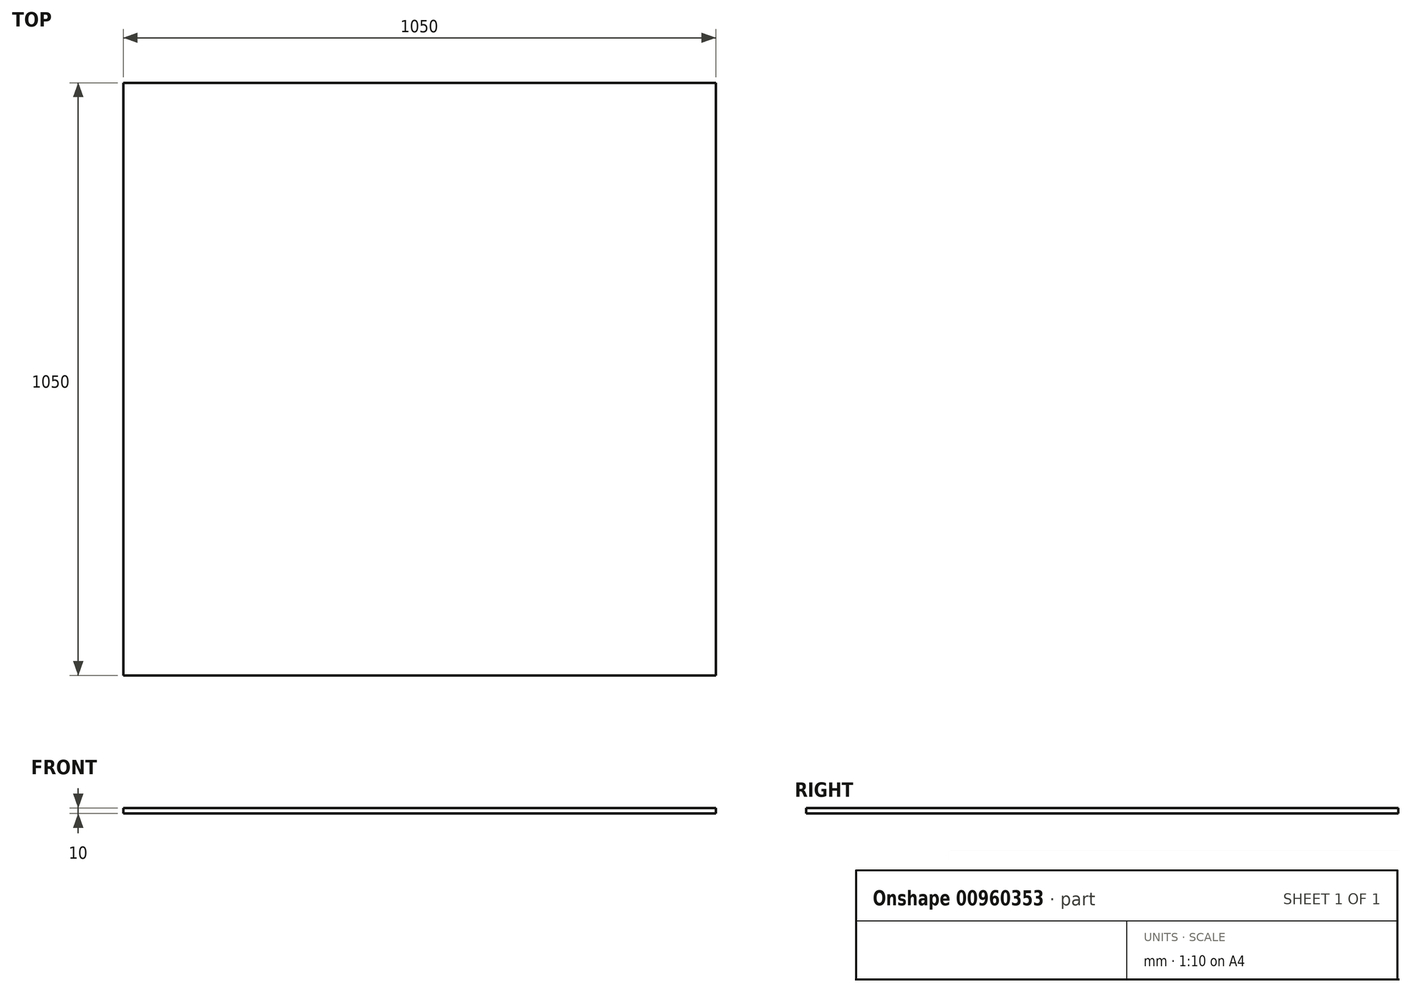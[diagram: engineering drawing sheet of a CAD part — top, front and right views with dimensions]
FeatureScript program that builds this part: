
annotation { "Feature Type Name" : "Feature", "Feature Type Description" : "" }
export const myFeature = defineFeature(function(context is Context, id is Id, definition is map)
    precondition{}
    {
        {
            var Q0;
            Q0=qCreatedBy(makeId("Top.planeOp"),FACE);
            var sketch = newSketch(context, id + "F0", { "sketchPlane" : qUnion([Q0])});
            skLineSegment(sketch, "E0.bottom", {"start": v(-525, 525) * mm, "end": v(525, 525) * mm});
            skLineSegment(sketch, "E0.top", {"start": v(-525, -525) * mm, "end": v(525, -525) * mm});
            skLineSegment(sketch, "E0.left", {"start": v(-525, 525) * mm, "end": v(-525, -525) * mm});
            skLineSegment(sketch, "E0.right", {"start": v(525, 525) * mm, "end": v(525, -525) * mm});
            skPoint(sketch, "E0.middle", {"position": v(0, 0) * mm});
            skSolve(sketch);
        }
        {
            var Q0;
            Q0 = qSketchRegion(id + "F0", true);
            extrude(context, id + "F1", {"entities" : qUnion([Q0]), "depth" : 10 * mm, "offsetDistance" : 25 * mm});
        }
    });
